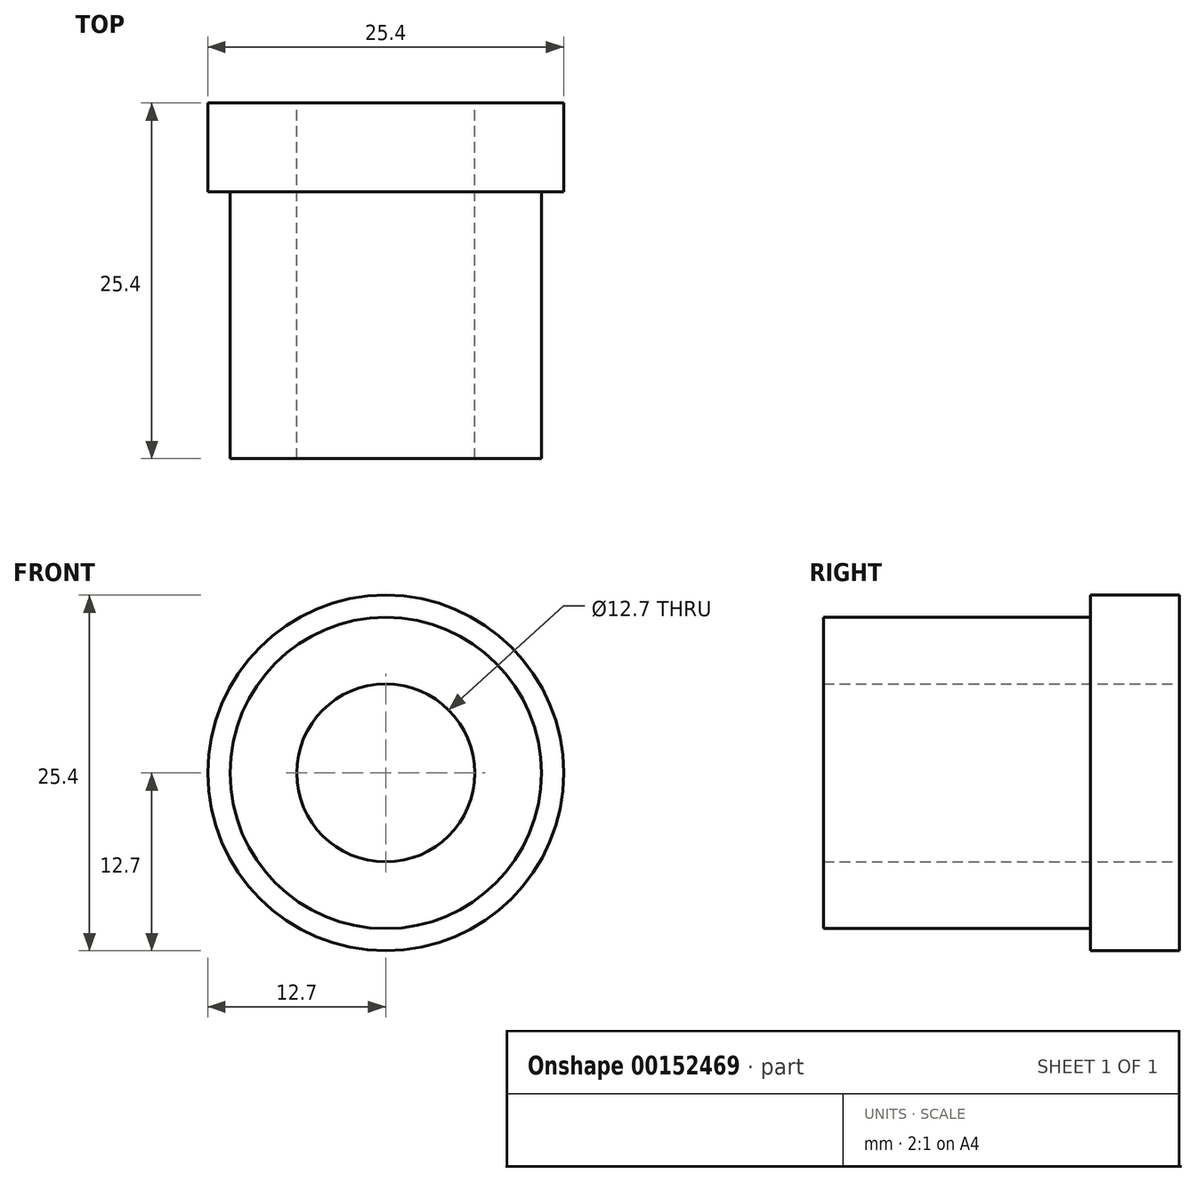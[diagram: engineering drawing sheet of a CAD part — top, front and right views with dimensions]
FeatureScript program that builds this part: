
annotation { "Feature Type Name" : "Feature", "Feature Type Description" : "" }
export const myFeature = defineFeature(function(context is Context, id is Id, definition is map)
    precondition{}
    {
        {
            var Q0;
            Q0=qCreatedBy(makeId("Front.planeOp"),FACE);
            var sketch = newSketch(context, id + "F0", { "sketchPlane" : qUnion([Q0])});
            skCircle(sketch, "E0", {"center": v(0, 0) * mm, "radius": 12.7 * mm});
            skCircle(sketch, "E1", {"center": v(0, 0) * mm, "radius": 6.35 * mm});
            skSolve(sketch);
        }
        {
            var Q0;
            Q0 = qSketchRegion(id + "F0", true);
            extrude(context, id + "F1", {"entities" : qUnion([Q0]), "depth" : 25.4 * mm});
        }
        {
            var Q0;
            Q0=qCreatedBy(makeId("Front.planeOp"),FACE);
            var sketch = newSketch(context, id + "F2", { "sketchPlane" : qUnion([Q0])});
            skCircle(sketch, "E2", {"center": v(0, 0) * mm, "radius": 3.38 * mm});
            skSolve(sketch);
        }
        {
            var Q0;
            Q0 = qSketchRegion(id + "F2", true);
            extrude(context, id + "F3", {"entities" : qUnion([Q0]), "depth" : 6.35 * mm});
        }
        {
            var Q0;
            Q0=makeQuery(id+"F3.opExtrude","CAP_FACE",FACE,{"disambiguationData":[OSD([sQuery(id+"F2.wireOp",EDGE,"E2")])],"isStart":false});
            var sketch = newSketch(context, id + "F4", { "sketchPlane" : qUnion([Q0])});
            skCircle(sketch, "E3", {"center": v(0, 0) * mm, "radius": 11.11 * mm});
            skCircle(sketch, "E4", {"center": v(0, 0) * mm, "radius": 12.7 * mm});
            skSolve(sketch);
        }
        {
            var Q0;
            Q0 = qSketchRegion(id + "F4", true);
            extrude(context, id + "F5", {"entities" : qUnion([Q0]), "operationType" : NewBodyOperationType.REMOVE, "depth" : 25.4 * mm});
        }
        {
            var Q0;
            Q0=makeQuery(id+"F3.opExtrude","CAP_FACE",FACE,{"disambiguationData":[OSD([sQuery(id+"F2.wireOp",EDGE,"E2")])],"isStart":false});
            var sketch = newSketch(context, id + "F6", { "sketchPlane" : qUnion([Q0])});
            skCircle(sketch, "E5", {"center": v(0, 0) * mm, "radius": 4.28 * mm});
            skSolve(sketch);
        }
        {
            var Q0;
            Q0 = qSketchRegion(id + "F6", true);
            extrude(context, id + "F7", {"entities" : qUnion([Q0]), "operationType" : NewBodyOperationType.REMOVE, "oppositeDirection" : true, "depth" : 25.4 * mm});
        }
    });
